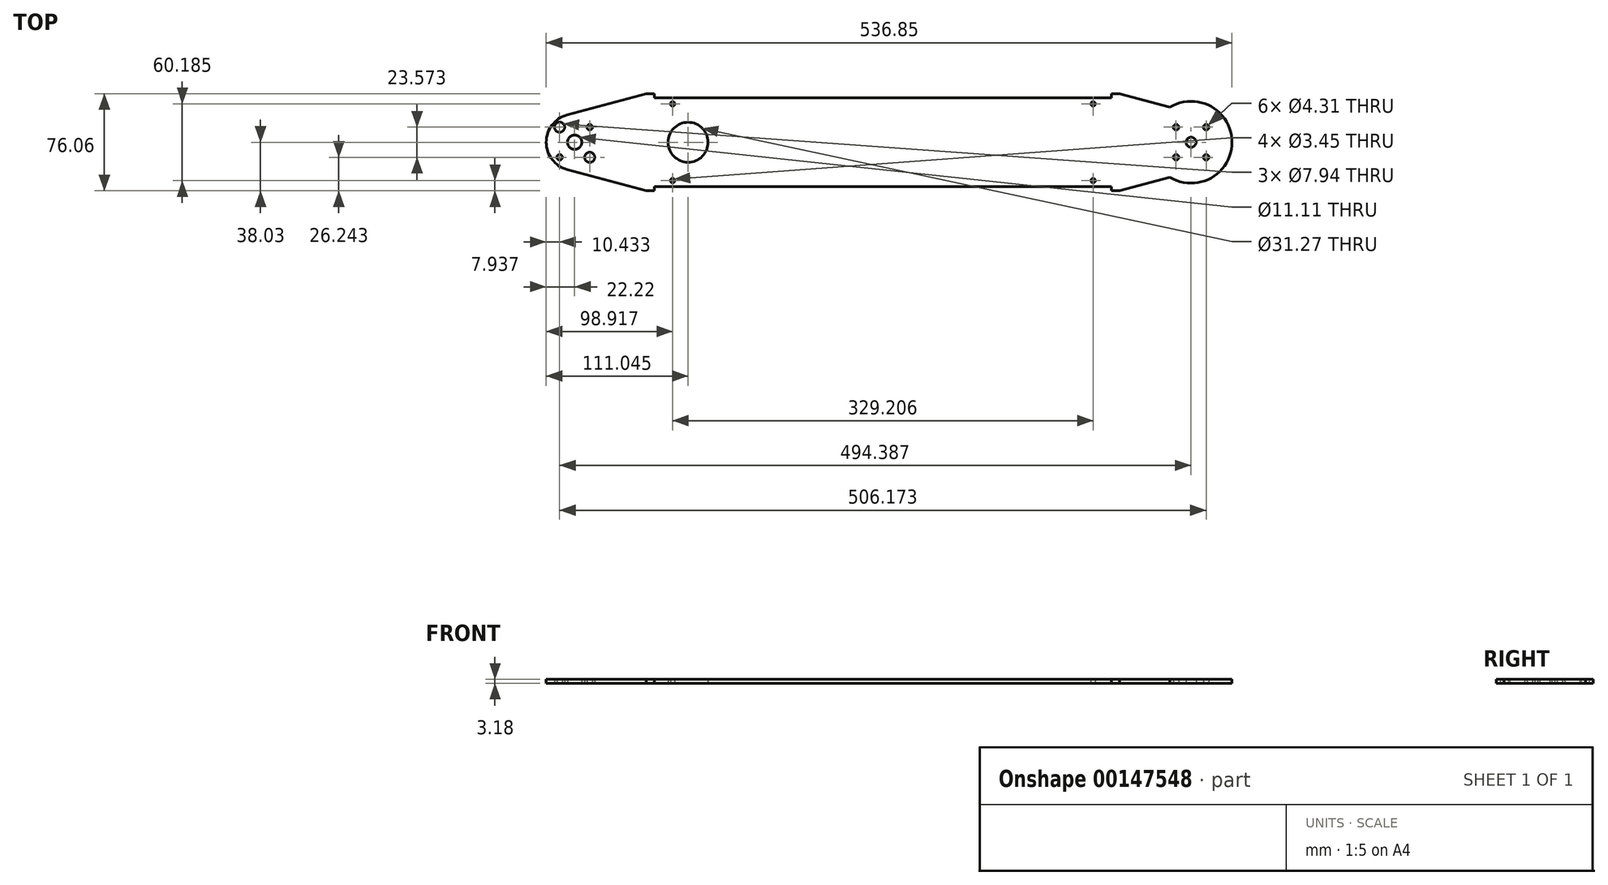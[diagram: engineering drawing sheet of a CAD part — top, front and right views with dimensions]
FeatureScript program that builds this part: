
annotation { "Feature Type Name" : "Feature", "Feature Type Description" : "" }
export const myFeature = defineFeature(function(context is Context, id is Id, definition is map)
    precondition{}
    {
        {
            var Q0;
            Q0=qCreatedBy(makeId("Top.planeOp"),FACE);
            var sketch = newSketch(context, id + "F0", { "sketchPlane" : qUnion([Q0])});
            skPoint(sketch, "E0.rect.middle", {"position": v(0, 0) * mm});
            skCircle(sketch, "E1", {"center": v(0, 0) * mm, "radius": 3.97 * mm});
            skLineSegment(sketch, "E2.bottom", {"start": v(11.79, 11.79) * mm, "end": v(-11.79, 11.79) * mm, "construction": true});
            skLineSegment(sketch, "E2.left", {"start": v(11.79, 11.79) * mm, "end": v(11.79, -11.79) * mm, "construction": true});
            skLineSegment(sketch, "E2.right", {"start": v(-11.79, 11.79) * mm, "end": v(-11.79, -11.79) * mm, "construction": true});
            skCircle(sketch, "E3", {"center": v(-11.79, 11.79) * mm, "radius": 2.15 * mm});
            skCircle(sketch, "E4", {"center": v(11.79, 11.79) * mm, "radius": 2.15 * mm});
            skCircle(sketch, "E5", {"center": v(11.79, -11.79) * mm, "radius": 2.15 * mm});
            skCircle(sketch, "E6", {"center": v(-11.79, -11.79) * mm, "radius": 2.15 * mm});
            skArc(sketch, "E7", {"start": v(-488.35, 21.47) * mm, "mid": v(-504.83, 0) * mm, "end": v(-488.35, -21.47) * mm});
            skLineSegment(sketch, "E8.bottom", {"start": v(-494.39, 11.79) * mm, "end": v(-470.81, 11.79) * mm, "construction": true});
            skLineSegment(sketch, "E8.top", {"start": v(-494.39, -11.79) * mm, "end": v(-470.81, -11.79) * mm, "construction": true});
            skLineSegment(sketch, "E8.left", {"start": v(-494.39, 11.79) * mm, "end": v(-494.39, -11.79) * mm, "construction": true});
            skLineSegment(sketch, "E8.right", {"start": v(-470.81, 11.79) * mm, "end": v(-470.81, -11.79) * mm, "construction": true});
            skCircle(sketch, "E9", {"center": v(-470.81, 11.79) * mm, "radius": 2.15 * mm});
            skCircle(sketch, "E10", {"center": v(-482.6, 0) * mm, "radius": 5.56 * mm});
            skCircle(sketch, "E11", {"center": v(-494.39, 11.79) * mm, "radius": 3.97 * mm});
            skCircle(sketch, "E12", {"center": v(-494.39, -11.79) * mm, "radius": 2.15 * mm});
            skCircle(sketch, "E13", {"center": v(-470.81, -11.79) * mm, "radius": 3.97 * mm});
            skLineSegment(sketch, "E14", {"start": v(0, 0) * mm, "end": v(-482.6, 0) * mm, "construction": true});
            skLineSegment(sketch, "E15", {"start": v(-488.35, -21.47) * mm, "end": v(-426.54, -38.03) * mm});
            skLineSegment(sketch, "E16", {"start": v(-488.35, 21.47) * mm, "end": v(-426.54, 38.03) * mm});
            skLineSegment(sketch, "E17", {"start": v(-420.2, -34.86) * mm, "end": v(-62.4, -34.86) * mm});
            skLineSegment(sketch, "E18", {"start": v(-420.2, 34.86) * mm, "end": v(-62.4, 34.86) * mm});
            skLineSegment(sketch, "E19", {"start": v(-420.2, 38.03) * mm, "end": v(-420.2, 34.86) * mm});
            skLineSegment(sketch, "E20", {"start": v(-420.2, 38.03) * mm, "end": v(-426.54, 38.03) * mm});
            skLineSegment(sketch, "E21", {"start": v(-420.2, -34.86) * mm, "end": v(-420.2, -38.03) * mm});
            skLineSegment(sketch, "E22", {"start": v(-420.2, -38.03) * mm, "end": v(-426.54, -38.03) * mm});
            skLineSegment(sketch, "E23", {"start": v(-62.4, -34.86) * mm, "end": v(-62.4, -38.03) * mm});
            skLineSegment(sketch, "E24", {"start": v(-62.4, -38.03) * mm, "end": v(-56.06, -38.03) * mm});
            skLineSegment(sketch, "E25", {"start": v(-62.4, 34.86) * mm, "end": v(-62.4, 38.03) * mm});
            skLineSegment(sketch, "E26", {"start": v(-62.4, 38.03) * mm, "end": v(-56.06, 38.03) * mm});
            skLineSegment(sketch, "E27", {"start": v(-56.06, -38.03) * mm, "end": v(-16.53, -27.44) * mm});
            skLineSegment(sketch, "E28", {"start": v(-16.53, 27.44) * mm, "end": v(-56.06, 38.03) * mm});
            skLineSegment(sketch, "E29", {"start": v(-420.2, 34.86) * mm, "end": v(-420.2, 30.1) * mm, "construction": true});
            skLineSegment(sketch, "E30", {"start": v(-420.2, 30.1) * mm, "end": v(-405.9, 30.1) * mm, "construction": true});
            skLineSegment(sketch, "E31", {"start": v(-420.2, -34.86) * mm, "end": v(-420.2, -30.1) * mm, "construction": true});
            skLineSegment(sketch, "E32", {"start": v(-420.2, -30.1) * mm, "end": v(-405.9, -30.1) * mm, "construction": true});
            skLineSegment(sketch, "E33", {"start": v(-62.4, -34.86) * mm, "end": v(-62.4, -30.1) * mm, "construction": true});
            skLineSegment(sketch, "E34", {"start": v(-62.4, -30.1) * mm, "end": v(-76.7, -30.1) * mm, "construction": true});
            skLineSegment(sketch, "E35", {"start": v(-62.4, 34.86) * mm, "end": v(-62.4, 30.1) * mm, "construction": true});
            skLineSegment(sketch, "E36", {"start": v(-62.4, 30.1) * mm, "end": v(-76.7, 30.1) * mm, "construction": true});
            skCircle(sketch, "E37", {"center": v(-405.9, 30.1) * mm, "radius": 1.73 * mm});
            skCircle(sketch, "E38", {"center": v(-76.7, 30.1) * mm, "radius": 1.73 * mm});
            skCircle(sketch, "E39", {"center": v(-76.7, -30.1) * mm, "radius": 1.73 * mm});
            skCircle(sketch, "E40", {"center": v(-405.9, -30.1) * mm, "radius": 1.73 * mm});
            skLineSegment(sketch, "E41", {"start": v(-11.79, -11.79) * mm, "end": v(11.79, -11.79) * mm, "construction": true});
            skLineSegment(sketch, "E42", {"start": v(-241.3, -34.86) * mm, "end": v(-241.3, 0) * mm, "construction": true});
            skLineSegment(sketch, "E43", {"start": v(-241.3, 0) * mm, "end": v(-241.3, 34.86) * mm, "construction": true});
            skArc(sketch, "E44", {"start": v(-16.53, -27.44) * mm, "mid": v(32.03, 0) * mm, "end": v(-16.53, 27.44) * mm});
            skLineSegment(sketch, "E45", {"start": v(-16.53, 27.44) * mm, "end": v(5.75, 21.47) * mm, "construction": true});
            skLineSegment(sketch, "E46", {"start": v(-16.53, -27.44) * mm, "end": v(5.75, -21.47) * mm, "construction": true});
            skArc(sketch, "E47", {"start": v(5.75, -21.47) * mm, "mid": v(22.23, 0) * mm, "end": v(5.75, 21.47) * mm, "construction": true});
            skCircle(sketch, "E48", {"center": v(-393.77, 0) * mm, "radius": 15.64 * mm});
            skLineSegment(sketch, "E49", {"start": v(5.75, 21.47) * mm, "end": v(-36.3, 21.47) * mm, "construction": true});
            skLineSegment(sketch, "E50", {"start": v(-36.3, 21.47) * mm, "end": v(-36.3, 32.73) * mm, "construction": true});
            skLineSegment(sketch, "E51", {"start": v(-488.35, 21.47) * mm, "end": v(-457.45, 21.47) * mm, "construction": true});
            skLineSegment(sketch, "E52", {"start": v(-457.45, 21.47) * mm, "end": v(-457.45, 29.75) * mm, "construction": true});
            skCircle(sketch, "E53", {"center": v(-494.39, 11.79) * mm, "radius": 5.56 * mm, "construction": true});
            skCircle(sketch, "E54", {"center": v(11.79, 11.79) * mm, "radius": 5.56 * mm, "construction": true});
            skSolve(sketch);
        }
        {
            var Q0;
            Q0=qSketchRegion(id+"F0",true);
            extrude(context, id + "F1", {"entities" : qUnion([Q0]), "depth" : 3.17 * mm});
        }
    });
